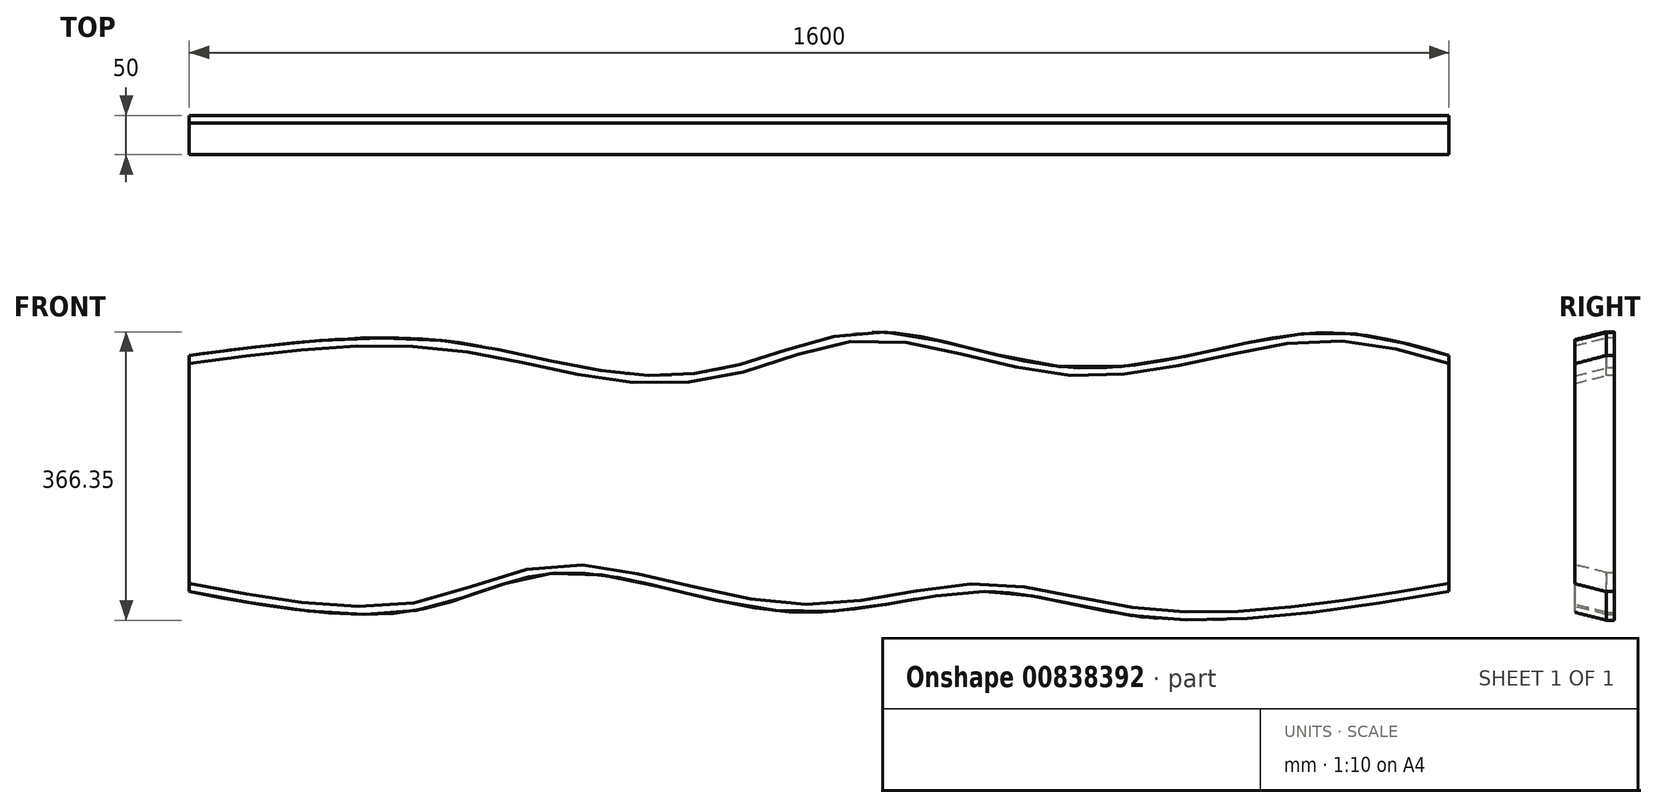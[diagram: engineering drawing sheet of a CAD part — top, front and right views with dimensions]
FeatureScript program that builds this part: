
annotation { "Feature Type Name" : "Feature", "Feature Type Description" : "" }
export const myFeature = defineFeature(function(context is Context, id is Id, definition is map)
    precondition{}
    {
        {
            var Q0;
            Q0=qCreatedBy(makeId("Front.planeOp"),FACE);
            var sketch = newSketch(context, id + "F0", { "sketchPlane" : qUnion([Q0])});
            skLineSegment(sketch, "E0.left", {"start": v(0, 0) * mm, "end": v(0, 300) * mm});
            skLineSegment(sketch, "E0.right", {"start": v(1600, 0) * mm, "end": v(1600, 300) * mm});
            skFitSpline(sketch, "E1", {"points": [v(0, 300) * mm, v(307.7, 320.09) * mm, v(527.64, 280.1) * mm, v(691.6, 286.1) * mm, v(871.54, 330.08) * mm, v(1133.47, 284.1) * mm, v(1421.39, 328.09) * mm, v(1600, 300) * mm], "startDerivative": vector(1922.7, 254.63) * mm, "endDerivative": vector(1313.88, -389.38) * mm});
            skFitSpline(sketch, "E2", {"points": [v(0, 0) * mm, v(287.71, -23.81) * mm, v(475.66, 24.17) * mm, v(765.57, -25.81) * mm, v(1007.5, 0) * mm, v(1227.44, -33.81) * mm, v(1600, 0) * mm], "startDerivative": vector(1720.78, -331.5) * mm, "endDerivative": vector(2011.07, 330.88) * mm});
            skSolve(sketch);
        }
        {
            var Q0;
            Q0 = qSketchRegion(id + "F0", true);
            extrude(context, id + "F1", {"entities" : qUnion([Q0]), "oppositeDirection" : true, "depth" : 50 * mm, "offsetDistance" : 25 * mm});
        }
        {
            var Q0;
            Q0=makeQuery(id+"F1.opExtrude","CAP_EDGE",EDGE,{"disambiguationData":[OSD([sQuery(id+"F0.wireOp",EDGE,"E1")])],"isStart":true});
            var Q1;
            Q1=makeQuery(id+"F1.opExtrude","CAP_EDGE",EDGE,{"disambiguationData":[OSD([sQuery(id+"F0.wireOp",EDGE,"E2")])],"isStart":true});
            chamfer(context, id + "F2", {"entities" : qUnion([Q0, Q1]), "chamferType" : ChamferType.TWO_OFFSETS, "width1" : 40 * mm, "oppositeDirection" : false, "width2" : 10 * mm, "tangentPropagation" : true});
        }
    });
